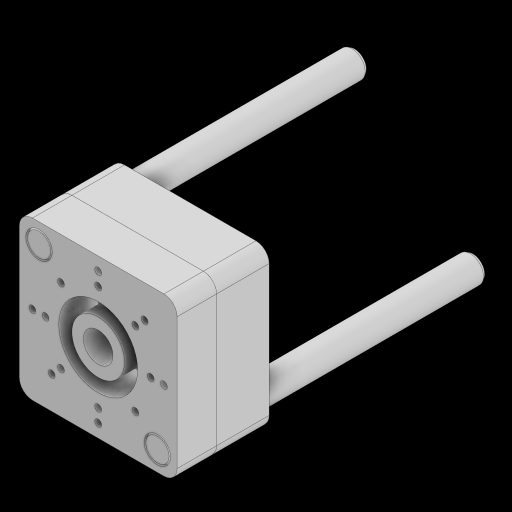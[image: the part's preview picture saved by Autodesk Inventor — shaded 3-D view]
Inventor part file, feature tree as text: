
AUTODESK INVENTOR PART (.ipt)
format: ipt  version: 2024 (Build 280153000, 153)  size: 591,872 bytes
history: native  units: mm
features: other x11, extrude x10, sketch x6, chamfer x5, hole x4, revolve x2, mirror x1, projected_geometry x1
ambient origin geometry x8: Origin, YZ Plane, XZ Plane, XY Plane, X Axis, Y Axis, Z Axis, Center Point
bodies: Body1 (feature_tree), Body2 (feature_tree), Body3 (feature_tree), Body4 (feature_tree), Body5 (feature_tree), Body6 (feature_tree), Body7 (feature_tree), Body8 (feature_tree), Body9 (feature_tree)
feature tree (40):
  other  "MP-plate movable"
  sketch  "Skizze1"  dims[d0=120.0mm d2=40.0mm d3=0.0mm]
  extrude  "Extrusion1"  Depth=40.0mm TaperAngle=0.0deg
  extrude  "Extrusion2"  Depth=20.0mm
  extrude  "Extrusion3"  Depth=15.0mm
  hole  "Bohrung1"  [1 undecoded]
  hole  "Bohrung2"  [1 undecoded]
  sketch  "Skizze2"  dims[d4=5.2mm d5=20.0mm]
  revolve  "Umdrehung1"
  chamfer  "Fasen1"  Distance=80.0mm Angle=360.0deg
  chamfer  "Fasen2"  Distance=60.0mm
  extrude  "Extrusion4"  Depth=30.0mm TaperAngle=0.0deg
  chamfer  "Fasen3"  Distance=240.0mm
  sketch  "Skizze3"  dims[d6=15.0mm d7=15.0mm]
  extrude  "Extrusion5"  Depth=3.0mm
  hole  "Bohrung3"  [1 undecoded]
  sketch  "Skizze4"  dims[d8=20.0mm d9=30.0mm]
  extrude  "Extrusion6"  TaperAngle=45.0deg  [1 undecoded]
  extrude  "Extrusion7"  TaperAngle=30.0deg  [1 undecoded]
  hole  "Bohrung4"  [1 undecoded]
  chamfer  "Fasen4"  Distance=40.0mm
  extrude  "Extrusion8"  TaperAngle=30.0deg  [1 undecoded]
  extrude  "Extrusion9"  Depth=4.0mm
  chamfer  "Fasen5"  Distance=4.0mm
  mirror  "Spiegeln1"
  revolve  "Umdrehung2"
  extrude  "Extrusion10"  Depth=3.0mm
  other  "MP-plate not movable"
  other  "MP-guidance"
  other  "MP-nozzle"
  other  "Anschlussfläche"
  other  "MP-pusher plate"
  projected_geometry  "Projizierte Kontur1"
  other  "MP-Pusher Mount"
  other  "MP-Mould Mount A"
  sketch  "Skizze5"  dims[d10=40.0mm d11=50.0mm d12=80.0mm d14=360.0deg]
  other  "Anordnung von MP-Mould Mount A:1"
  other  "MP-Mould Mount B"
  sketch  "Skizze6"  dims[d16=10.0mm d17=60.0mm d18=30.0mm d19=0.0mm d20=240.0mm d21=0.0mm d22=5.2mm d23=6.0mm d24=4.0mm d25=2.0mm d26=90.0deg d27=8.0mm d28=20.594885mm d29=5.2mm d30=6.0mm d31=4.0mm d32=2.0mm d33=90.0deg d34=8.0mm d35=20.594885mm d36=3.0mm d37=1.0mm d38=45.0deg d39=30.0deg d40=8.0mm d42=40.0mm d43=30.0deg d44=4.0mm d45=4.0mm d46=2.5mm d47=4.5mm d48=0.872665mm d49=50.0mm d50=2.0mm d51=10.0mm d52=90.0deg d53=90.0deg d54=2.0mm d55=2.0mm d56=30.0deg d57=2.0mm d58=2.0mm d59=30.0deg d60=80.0mm d61=10.0mm d62=0.0mm d63=5.0mm d64=2.0mm d65=30.0deg d66=3.63961mm d67=100.0mm d68=16.0mm d69=10.0mm d70=0.0mm d71=5.5mm d72=6.0mm d73=11.0mm d74=4.0mm d75=14.3117mm d76=8.0mm d77=20.594885mm d78=16.0mm d79=16.0mm d80=16.0mm d81=16.0mm d82=64.0mm d84=5.0mm d85=20.0mm d86=0.0mm d87=11.8mm d88=0.0mm d89=4.134mm d90=10.0mm d91=10.0mm d92=2.0mm d93=90.0deg d94=14.2mm d95=0.0mm d96=90.0deg d97=0.5mm d98=2.0mm d99=45.0deg d100=6.0mm d101=3.0mm d102=0.0mm d103=3.0mm d104=0.0mm d105=1.5mm d106=2.0mm d107=45.0deg d108=0.0mm d109=0.0mm d110=9.0mm]
  other  "Rotationsfläche1"
note: 7 required parameter values undecoded (feature->parameter linkage not recoverable at this tier; creation-order binding heuristic only, values carry confidence <= 0.55)
